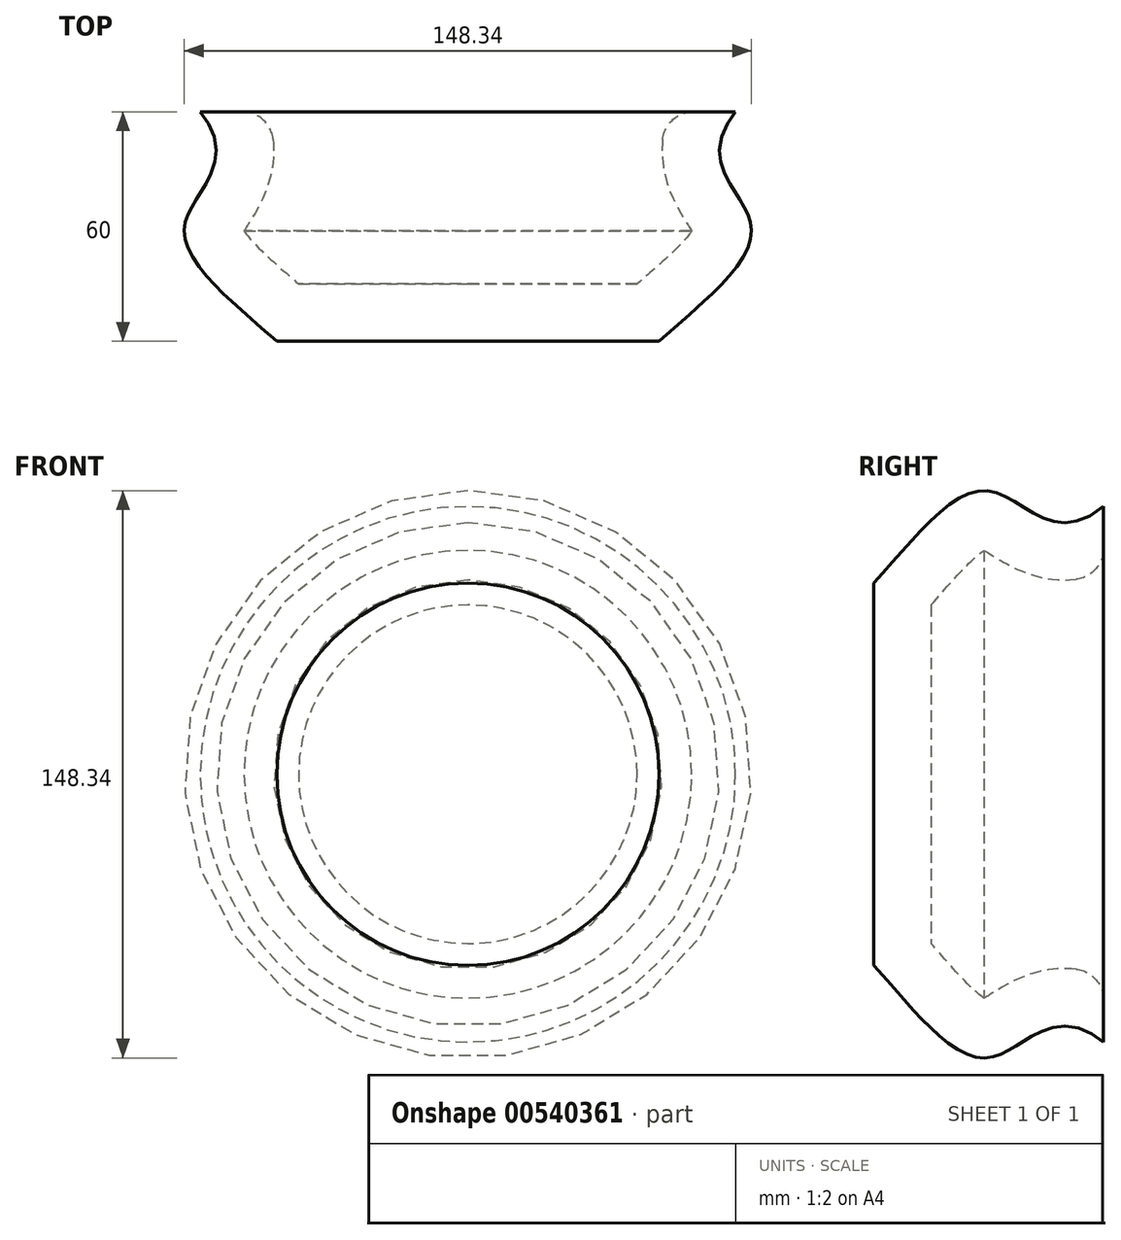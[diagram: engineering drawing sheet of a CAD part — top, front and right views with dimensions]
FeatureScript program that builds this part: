
annotation { "Feature Type Name" : "Feature", "Feature Type Description" : "" }
export const myFeature = defineFeature(function(context is Context, id is Id, definition is map)
    precondition{}
    {
        {
            var Q0;
            Q0=qCreatedBy(makeId("Top.planeOp"),FACE);
            var sketch = newSketch(context, id + "F0", { "sketchPlane" : qUnion([Q0])});
            skLineSegment(sketch, "E0", {"start": v(0, 0) * mm, "end": v(-50, 0) * mm});
            skLineSegment(sketch, "E1", {"start": v(0, 60) * mm, "end": v(-70, 60) * mm});
            skFitSpline(sketch, "E2", {"points": [v(-50, 0) * mm, v(-74.09, 30.18) * mm, v(-70, 60) * mm], "startDerivative": vector(-59.7, 55.03) * mm, "endDerivative": vector(-70.42, 85.44) * mm});
            skLineSegment(sketch, "E3", {"start": v(0, 60) * mm, "end": v(0, 0) * mm});
            skSolve(sketch);
        }
        {
            var Q0;
            Q0=makeQuery(id+"F0.imprint","IMPRINT",FACE,{"disambiguationData":[TD([[makeQuery(id+"F0.imprint","IMPRINT",EDGE,{"derivedFrom":sQuery(id+"F0.wireOp",EDGE,"E0")}),-1.0]])]});
            var Q1;
            Q1=sQuery(id+"F0.wireOp",EDGE,"E3");
            revolve(context, id + "F1", {"entities" : qUnion([Q0]), "axis" : qUnion([Q1]), "revolveType" : RevolveType.FULL});
        }
        {
            var Q0;
            Q0=makeQuery(id+"F1.opRevolve","SWEPT_FACE",FACE,{"disambiguationData":[OSD([sQuery(id+"F0.wireOp",EDGE,"E1")])]});
            shell(context, id + "F2", {"entities" : qUnion([Q0]), "thickness" : 15 * mm});
        }
        {
            var Q0;
            Q0=makeQuery(id+"F2.opShell","OFFSET_EDGE",EDGE,{"disambiguationData":[OSD([sQuery(id+"F0.wireOp",EDGE,"E1"),sQuery(id+"F0.wireOp",EDGE,"E2")])]});
            fillet(context, id + "F3", {"entities" : qUnion([Q0]), "radius" : 8 * mm, "tangentPropagation" : true, "allowEdgeOverflow" : false});
        }
    });
